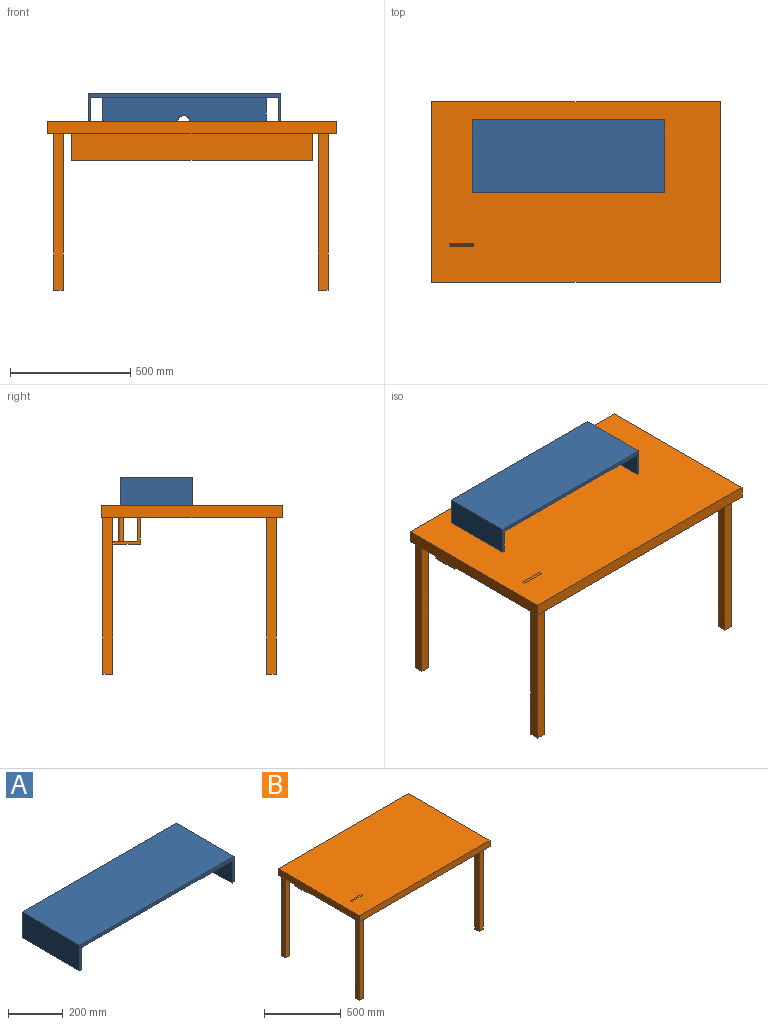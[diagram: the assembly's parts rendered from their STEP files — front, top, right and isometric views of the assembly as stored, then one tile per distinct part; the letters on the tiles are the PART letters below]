
ASSEMBLY  parts=2 mates=1
PART A: 21 faces, bbox 800x300x115 mm
  f0: plane 293.09x10mm, normal (0,0,-1), area 2930.9mm2, adj f13,f15,f17,f20
  f1: plane 299.83x10mm, normal (0,0,-1), area 2998.2mm2, adj f13,f15,f18,f19
  f2: plane 800x300mm, normal (0,0,1), area 240000mm2, adj f3,f9,f10,f11
  f3: plane 300x115mm, normal (-1,0,0), area 34500mm2, adj f2,f4,f10,f11
  f4: plane 300x10mm, normal (0,0,-1), area 3000mm2, adj f3,f5,f10,f11
  f5: plane 300x100mm, normal (1,0,0), area 30000mm2, adj f4,f6,f10,f11
  f6: plane 780x300mm, normal (0,0,-1), area 227200mm2, adj f5,f7,f10,f11,f12,f13,f14,f15
  f7: plane 300x100mm, normal (-1,0,0), area 30000mm2, adj f6,f8,f10,f11
  f8: plane 300x10mm, normal (0,0,-1), area 3000mm2, adj f7,f9,f10,f11
  f9: plane 300x115mm, normal (1,0,0), area 34500mm2, adj f2,f8,f10,f11
  f10: plane 800x115mm, normal (0,-1,0), area 14000mm2, adj f2,f3,f4,f5,f6,f7,f8,f9
  f11: plane 800x115mm, normal (0,1,0), area 14000mm2, adj f2,f3,f4,f5,f6,f7,f8,f9
  f12: plane 90x10mm, normal (-1,0,0), area 900mm2, adj f6,f13,f15,f20
  f13: plane 680x100mm, normal (0,1,0), area 66949.1mm2, adj f0,f1,f6,f12,f14,f16,f17,f18
  f14: plane 90x10mm, normal (1,0,0), area 900mm2, adj f6,f13,f15,f19
  f15: plane 680x100mm, normal (0,-1,0), area 66949.1mm2, adj f0,f1,f6,f12,f14,f16,f17,f18
  f16: cylinder r=25mm len=47.92mm, axis (0,1,0), area 640.5mm2, adj f13,f15,f17,f18
  f17: cylinder r=10mm len=10mm, axis (0,1,0), area 128.1mm2, adj f0,f13,f15,f16
  f18: cylinder r=10mm len=10mm, axis (0,1,0), area 128.1mm2, adj f1,f13,f15,f16
  f19: cylinder r=10mm len=10mm, axis (0,1,0), area 157.1mm2, adj f1,f13,f14,f15
  f20: cylinder r=10mm len=10mm, axis (0,-1,0), area 157.1mm2, adj f0,f12,f13,f15
PART B: 42 faces, bbox 1200x750x700 mm
  f0: plane 1200x750mm, normal (0,0,1), area 898845.3mm2, adj f2,f3,f4,f5,f37,f39,f40,f41
  f1: plane 1200x750mm, normal (0,0,-1), area 882343.4mm2, adj f2,f3,f4,f5,f7,f8,f11,f12
  f2: plane 750x50mm, normal (1,0,0), area 37500mm2, adj f0,f1,f4,f5
  f3: plane 750x50mm, normal (-1,0,0), area 37500mm2, adj f0,f1,f4,f5
  f4: plane 1200x50mm, normal (0,1,0), area 60000mm2, adj f0,f1,f2,f3
  f5: plane 1200x50mm, normal (0,-1,0), area 60000mm2, adj f0,f1,f2,f3
  f6: plane 1000x100mm, normal (0,0,1), area 98743.4mm2, adj f7,f10,f11,f12,f13,f14,f15,f16
  f7: plane 1000x100mm, normal (0,1,0), area 100000mm2, adj f1,f6,f11,f12
  f8: plane 1000x110mm, normal (0,-1,0), area 110000mm2, adj f1,f9,f11,f12
  f9: plane 1000x110mm, normal (0,0,-1), area 110000mm2, adj f8,f10,f11,f12
  f10: plane 1000x10mm, normal (0,1,0), area 10000mm2, adj f6,f9,f11,f12
  f11: plane 110x110mm, normal (-1,0,0), area 2100mm2, adj f1,f6,f7,f8,f9,f10
  f12: plane 110x110mm, normal (1,0,0), area 2100mm2, adj f1,f6,f7,f8,f9,f10
  f13: cylinder r=10mm len=100mm, axis (0,0,-1), area 6283.2mm2, adj f1,f6
  f14: cylinder r=10mm len=100mm, axis (0,0,-1), area 6283.2mm2, adj f1,f6
  f15: cylinder r=10mm len=100mm, axis (0,0,-1), area 6283.2mm2, adj f1,f6
  f16: cylinder r=10mm len=100mm, axis (0,0,-1), area 6283.2mm2, adj f1,f6
  f17: plane 650x40mm, normal (0,-1,0), area 26000mm2, adj f1,f18,f20,f21
  f18: plane 650x40mm, normal (-1,0,0), area 26000mm2, adj f1,f17,f19,f21
  f19: plane 650x40mm, normal (0,1,0), area 26000mm2, adj f1,f18,f20,f21
  f20: plane 650x40mm, normal (1,0,0), area 26000mm2, adj f1,f17,f19,f21
  f21: plane 40x40mm, normal (0,0,-1), area 1600mm2, adj f17,f18,f19,f20
  f22: plane 650x40mm, normal (0,-1,0), area 26000mm2, adj f1,f23,f25,f26
  f23: plane 650x40mm, normal (-1,0,0), area 26000mm2, adj f1,f22,f24,f26
  f24: plane 650x40mm, normal (0,1,0), area 26000mm2, adj f1,f23,f25,f26
  f25: plane 650x40mm, normal (1,0,0), area 26000mm2, adj f1,f22,f24,f26
  f26: plane 40x40mm, normal (0,0,-1), area 1600mm2, adj f22,f23,f24,f25
  f27: plane 650x40mm, normal (0,-1,0), area 26000mm2, adj f1,f28,f30,f31
  f28: plane 650x40mm, normal (-1,0,0), area 26000mm2, adj f1,f27,f29,f31
  f29: plane 650x40mm, normal (0,1,0), area 26000mm2, adj f1,f28,f30,f31
  f30: plane 650x40mm, normal (1,0,0), area 26000mm2, adj f1,f27,f29,f31
  f31: plane 40x40mm, normal (0,0,-1), area 1600mm2, adj f27,f28,f29,f30
  f32: plane 650x40mm, normal (0,-1,0), area 26000mm2, adj f1,f33,f35,f36
  f33: plane 650x40mm, normal (-1,0,0), area 26000mm2, adj f1,f32,f34,f36
  f34: plane 650x40mm, normal (0,1,0), area 26000mm2, adj f1,f33,f35,f36
  f35: plane 650x40mm, normal (1,0,0), area 26000mm2, adj f1,f32,f34,f36
  f36: plane 40x40mm, normal (0,0,-1), area 1600mm2, adj f32,f33,f34,f35
  f37: plane 100x22.32mm, normal (0,-0.87,0.5), area 2577.4mm2, adj f0,f38,f40,f41
  f38: plane 100x8.66mm, normal (0,0.5,0.87), area 1000mm2, adj f37,f39,f40,f41
  f39: plane 100x17.32mm, normal (0,0.87,-0.5), area 2000mm2, adj f0,f38,f40,f41
  f40: plane 22.32x21.55mm, normal (-1,0,0), area 228.9mm2, adj f0,f37,f38,f39
  f41: plane 22.32x21.55mm, normal (1,0,0), area 228.9mm2, adj f0,f37,f38,f39
PLACE A t=(-14.24,131.91,-51.6)mm
PLACE B t=(20.9,-542.05,-76.6)mm fixed
MATE parallel A.f9 <-> B.f2  axis (1,0,0) through (389.13,-18.09,5.9)mm
